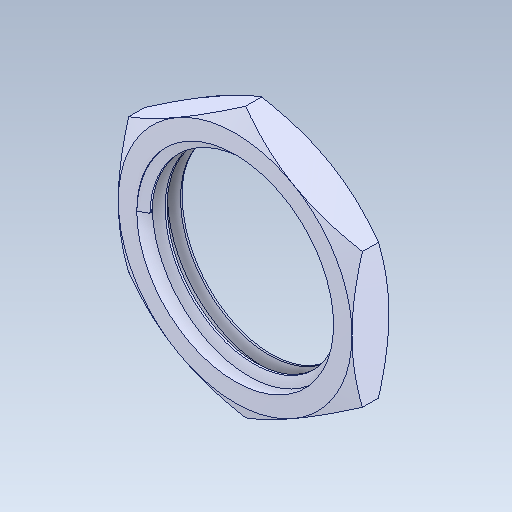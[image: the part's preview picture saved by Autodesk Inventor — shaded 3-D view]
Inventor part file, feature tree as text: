
AUTODESK INVENTOR PART (.ipt)
format: ipt  version: 2020 (Build 240168000, 168)  size: 221,696 bytes
history: mixed  units: mm
features: other x1, thread x1, imported_body x1
ambient origin geometry x8: Origin, YZ Plane, XZ Plane, XY Plane, X Axis, Y Axis, Z Axis, Center Point
bodies: Body1 (imported_parasolid)
feature tree (3):
  other  "Bryła1"
  thread  "Thread1"  [1 undecoded]
  imported_body  NMx_Import_Brep_tag  [imported B-rep: ~5 faces, bbox_mm=None]
note: 1 required parameter value undecoded (feature->parameter linkage not recoverable at this tier; creation-order binding heuristic only, values carry confidence <= 0.55)
